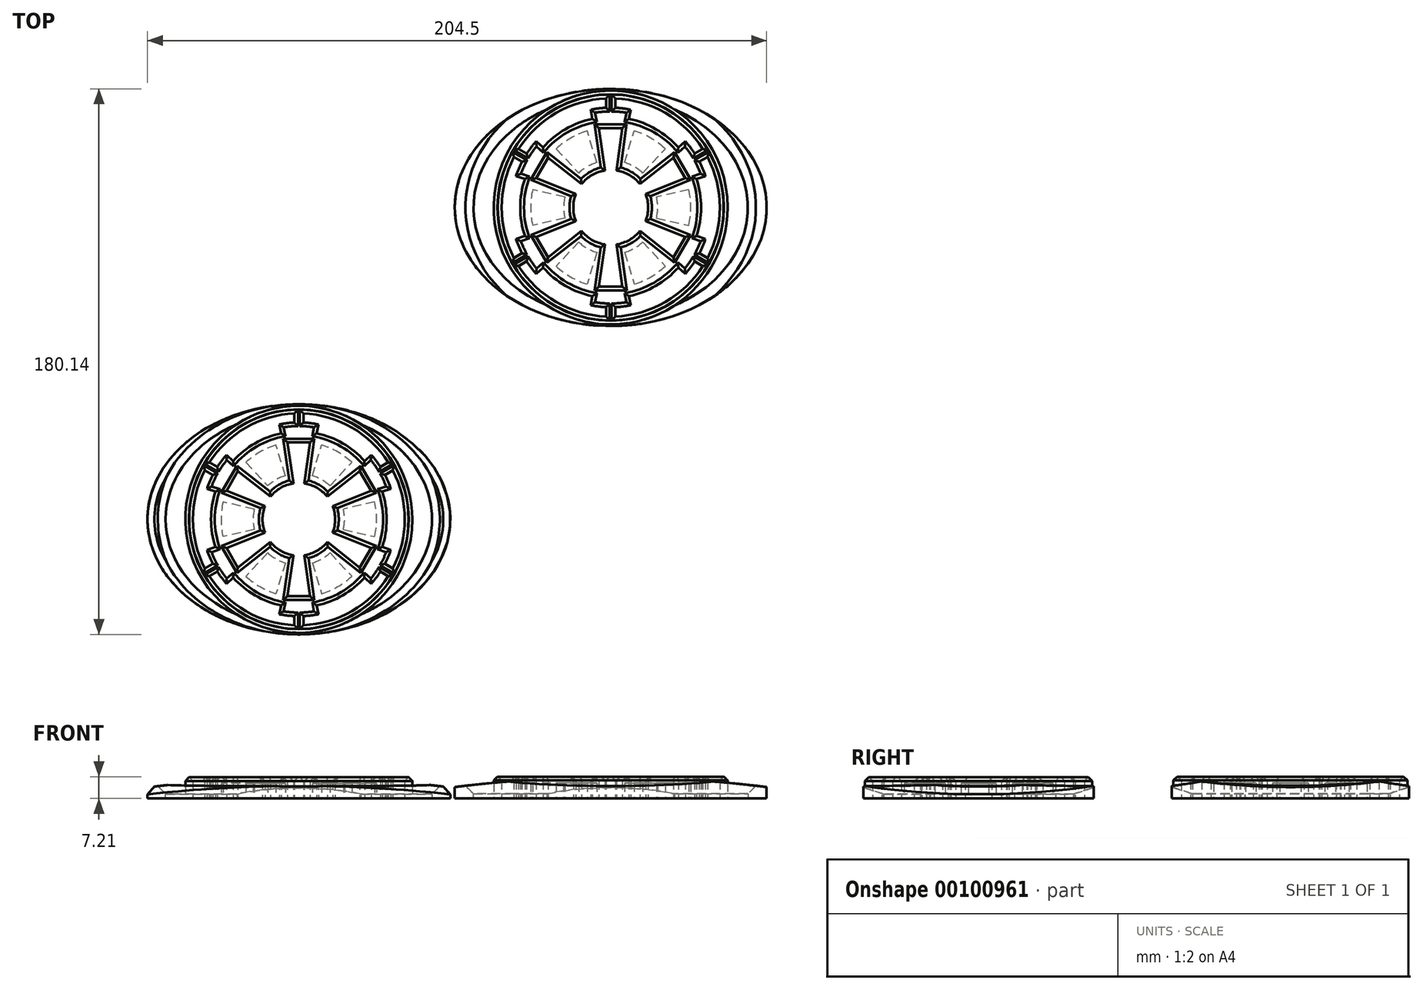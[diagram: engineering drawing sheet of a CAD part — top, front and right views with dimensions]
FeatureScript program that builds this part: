
annotation { "Feature Type Name" : "Feature", "Feature Type Description" : "" }
export const myFeature = defineFeature(function(context is Context, id is Id, definition is map)
    precondition{}
    {
        {
            var Q0;
            Q0=qCreatedBy(makeId("Top.planeOp"),FACE);
            var sketch = newSketch(context, id + "F0", { "sketchPlane" : qUnion([Q0])});
            skEllipse(sketch, "E0", {"center": v(0, 0) * mm, "majorRadius": 38 * mm, "minorRadius": 50 * mm, "majorAxis": v(0, 1)});
            skEllipse(sketch, "E1", {"center": v(0, 0) * mm, "majorRadius": 35.5 * mm, "minorRadius": 44 * mm, "majorAxis": v(0, 1)});
            skSolve(sketch);
        }
        {
            var Q0;
            Q0 = qSketchRegion(id + "F0", true);
            extrude(context, id + "F1", {"entities" : qUnion([Q0]), "depth" : 7 * mm});
        }
        {
            var Q0;
            Q0=makeQuery(id+"F1.opExtrude","CAP_EDGE",EDGE,{"disambiguationData":[OSD([sQuery(id+"F0.wireOp",EDGE,"E1")])],"isStart":false});
            chamfer(context, id + "F2", {"entities" : qUnion([Q0]), "width" : 5.5 * mm, "tangentPropagation" : true});
        }
        {
            var Q0;
            Q0=qCreatedBy(makeId("Front.planeOp"),FACE);
            var sketch = newSketch(context, id + "F3", { "sketchPlane" : qUnion([Q0])});
            skPoint(sketch, "E2.middle", {"position": v(0, 0) * mm});
            skArc(sketch, "E3", {"start": v(50.97, 3.54) * mm, "mid": v(0, 6.8) * mm, "end": v(-50.97, 3.54) * mm});
            skLineSegment(sketch, "E4.top", {"start": v(-50.97, 12) * mm, "end": v(50.97, 12) * mm});
            skLineSegment(sketch, "E4.left", {"start": v(-50.97, 3.54) * mm, "end": v(-50.97, 12) * mm});
            skLineSegment(sketch, "E4.right", {"start": v(50.97, 3.54) * mm, "end": v(50.97, 12) * mm});
            skPoint(sketch, "E2.right.end.orphan", {"position": v(-50.97, -3.54) * mm});
            skPoint(sketch, "E2.left.end.orphan", {"position": v(50.97, -3.54) * mm});
            skSolve(sketch);
        }
        {
            var Q0;
            Q0 = qSketchRegion(id + "F3", true);
            extrude(context, id + "F4", {"entities" : qUnion([Q0]), "operationType" : NewBodyOperationType.REMOVE, "endBound" : BoundingType.SYMMETRIC, "oppositeDirection" : true, "depth" : 100 * mm});
        }
        {
            var Q0;
            Q0=qCreatedBy(makeId("Top.planeOp"),FACE);
            var sketch = newSketch(context, id + "F5", { "sketchPlane" : qUnion([Q0])});
            skArc(sketch, "E5", {"start": v(0, 37.5) * mm, "mid": v(-35.71, 11.45) * mm, "end": v(-21.8, -30.51) * mm});
            skArc(sketch, "E6", {"start": v(-31.03, 16.18) * mm, "mid": v(-35, 0) * mm, "end": v(-31.03, -16.18) * mm});
            skLineSegment(sketch, "E7.left", {"start": v(-1.5, 34.98) * mm, "end": v(-1.5, 31.96) * mm});
            skLineSegment(sketch, "E7.right", {"start": v(1.5, 34.98) * mm, "end": v(1.5, 31.96) * mm});
            skLineSegment(sketch, "E8.1.0", {"start": v(-31.03, -16.18) * mm, "end": v(-28.43, -14.68) * mm});
            skLineSegment(sketch, "E8.1.1", {"start": v(-29.53, -18.78) * mm, "end": v(-26.93, -17.28) * mm});
            skLineSegment(sketch, "E8.2.0", {"start": v(29.53, -18.78) * mm, "end": v(26.93, -17.28) * mm});
            skLineSegment(sketch, "E8.2.1", {"start": v(31.03, -16.18) * mm, "end": v(28.43, -14.68) * mm});
            skArc(sketch, "E9", {"start": v(-28.43, 14.68) * mm, "mid": v(-29.37, 12.7) * mm, "end": v(-30.17, 10.66) * mm});
            skArc(sketch, "E10", {"start": v(-27.52, 9.14) * mm, "mid": v(-29, 0) * mm, "end": v(-27.52, -9.14) * mm});
            skPoint(sketch, "E11.orphan", {"position": v(-31.93, 16.7) * mm});
            skPoint(sketch, "E12.orphan", {"position": v(-30.43, 19.3) * mm});
            skPoint(sketch, "E13.orphan", {"position": v(-28.25, 23.07) * mm});
            skLineSegment(sketch, "E14.trimOffspring", {"start": v(-26.93, 17.28) * mm, "end": v(-29.53, 18.78) * mm});
            skLineSegment(sketch, "E15.trimOffspring", {"start": v(-28.43, 14.68) * mm, "end": v(-31.03, 16.18) * mm});
            skArc(sketch, "E16.trimOffspring", {"start": v(-30.17, -10.66) * mm, "mid": v(-29.37, -12.7) * mm, "end": v(-28.43, -14.68) * mm});
            skArc(sketch, "E17.trimOffspring", {"start": v(-24.32, 20.8) * mm, "mid": v(-25.69, 19.08) * mm, "end": v(-26.93, 17.28) * mm});
            skPoint(sketch, "E18.orphan", {"position": v(-5.85, 36) * mm});
            skPoint(sketch, "E19.orphan", {"position": v(1.5, 36) * mm});
            skPoint(sketch, "E20.orphan", {"position": v(-1.5, 36) * mm});
            skPoint(sketch, "E21.orphan", {"position": v(5.85, 36) * mm});
            skArc(sketch, "E22.trimOffspring", {"start": v(-21.8, -30.51) * mm, "mid": v(35.71, -11.45) * mm, "end": v(0, 37.5) * mm});
            skArc(sketch, "E23.trimOffspring", {"start": v(5.85, 31.46) * mm, "mid": v(3.68, 31.79) * mm, "end": v(1.5, 31.96) * mm});
            skArc(sketch, "E24.trimOffspring", {"start": v(-5.85, 28.4) * mm, "mid": v(-14.5, 25.11) * mm, "end": v(-21.67, 19.27) * mm});
            skArc(sketch, "E25.trimOffspring", {"start": v(-1.5, 34.97) * mm, "mid": v(-17.5, 30.31) * mm, "end": v(-29.53, 18.78) * mm});
            skArc(sketch, "E26.trimOffspring", {"start": v(-1.5, 31.96) * mm, "mid": v(-3.68, 31.79) * mm, "end": v(-5.85, 31.46) * mm});
            skArc(sketch, "E27.trimOffspring", {"start": v(21.67, 19.27) * mm, "mid": v(14.5, 25.11) * mm, "end": v(5.85, 28.4) * mm});
            skPoint(sketch, "E28.orphan", {"position": v(30.43, 19.3) * mm});
            skPoint(sketch, "E29.orphan", {"position": v(31.93, 16.7) * mm});
            skPoint(sketch, "E30.orphan", {"position": v(34.1, 12.93) * mm});
            skLineSegment(sketch, "E31.trimOffspring", {"start": v(26.93, 17.28) * mm, "end": v(29.53, 18.78) * mm});
            skLineSegment(sketch, "E32.trimOffspring", {"start": v(28.43, 14.68) * mm, "end": v(31.03, 16.18) * mm});
            skArc(sketch, "E33.trimOffspring", {"start": v(26.93, 17.28) * mm, "mid": v(25.69, 19.08) * mm, "end": v(24.32, 20.8) * mm});
            skArc(sketch, "E34.trimOffspring", {"start": v(29.53, 18.78) * mm, "mid": v(17.5, 30.31) * mm, "end": v(1.5, 34.97) * mm});
            skArc(sketch, "E35.trimOffspring", {"start": v(30.17, 10.66) * mm, "mid": v(29.37, 12.7) * mm, "end": v(28.43, 14.68) * mm});
            skPoint(sketch, "E36.orphan", {"position": v(34.1, -12.93) * mm});
            skArc(sketch, "E37.trimOffspring", {"start": v(27.52, -9.14) * mm, "mid": v(29, 0) * mm, "end": v(27.52, 9.14) * mm});
            skArc(sketch, "E38.trimOffspring", {"start": v(28.43, -14.68) * mm, "mid": v(29.37, -12.7) * mm, "end": v(30.17, -10.66) * mm});
            skPoint(sketch, "E39.orphan", {"position": v(31.93, -16.7) * mm});
            skPoint(sketch, "E40.orphan", {"position": v(30.43, -19.3) * mm});
            skArc(sketch, "E41.trimOffspring", {"start": v(24.32, -20.8) * mm, "mid": v(25.69, -19.08) * mm, "end": v(26.93, -17.28) * mm});
            skArc(sketch, "E42.trimOffspring", {"start": v(5.85, -28.4) * mm, "mid": v(14.5, -25.11) * mm, "end": v(21.67, -19.27) * mm});
            skLineSegment(sketch, "E43.trimOffspring", {"start": v(-1.5, -31.96) * mm, "end": v(-1.5, -34.98) * mm});
            skLineSegment(sketch, "E44.trimOffspring", {"start": v(1.5, -31.96) * mm, "end": v(1.5, -34.97) * mm});
            skArc(sketch, "E45.trimOffspring", {"start": v(1.5, -31.96) * mm, "mid": v(3.68, -31.79) * mm, "end": v(5.85, -31.46) * mm});
            skPoint(sketch, "E46.orphan", {"position": v(5.85, -36) * mm});
            skArc(sketch, "E47.trimOffspring", {"start": v(1.5, -34.97) * mm, "mid": v(17.5, -30.31) * mm, "end": v(29.53, -18.78) * mm});
            skPoint(sketch, "E48.orphan", {"position": v(-1.5, -36) * mm});
            skPoint(sketch, "E49.trimOffspring.end.orphan", {"position": v(-5.85, -36) * mm});
            skPoint(sketch, "E50.top.end.orphan", {"position": v(1.5, -36) * mm});
            skPoint(sketch, "E51.orphan", {"position": v(-34.1, -12.93) * mm});
            skPoint(sketch, "E52.orphan", {"position": v(-31.93, -16.7) * mm});
            skPoint(sketch, "E53.orphan", {"position": v(-30.43, -19.3) * mm});
            skPoint(sketch, "E54.orphan", {"position": v(-28.25, -23.07) * mm});
            skArc(sketch, "E55.trimOffspring", {"start": v(-29.53, -18.78) * mm, "mid": v(-17.5, -30.31) * mm, "end": v(-1.5, -34.97) * mm});
            skArc(sketch, "E56.trimOffspring", {"start": v(-26.93, -17.28) * mm, "mid": v(-25.69, -19.08) * mm, "end": v(-24.32, -20.8) * mm});
            skArc(sketch, "E57.trimOffspring", {"start": v(-21.67, -19.27) * mm, "mid": v(-14.5, -25.11) * mm, "end": v(-5.85, -28.4) * mm});
            skArc(sketch, "E58", {"start": v(-1.82, 11.86) * mm, "mid": v(-6, 10.4) * mm, "end": v(-9.36, 7.5) * mm});
            skLineSegment(sketch, "E59.bottom", {"start": v(-3.75, 25.42) * mm, "end": v(3.75, 25.42) * mm});
            skLineSegment(sketch, "E59.top", {"start": v(-3.75, -25.42) * mm, "end": v(3.75, -25.42) * mm});
            skLineSegment(sketch, "E60", {"start": v(-3.75, 25.42) * mm, "end": v(-1.82, 11.86) * mm});
            skLineSegment(sketch, "E61", {"start": v(3.75, 25.42) * mm, "end": v(1.82, 11.86) * mm});
            skLineSegment(sketch, "E62", {"start": v(-3.75, -25.42) * mm, "end": v(-1.82, -11.86) * mm});
            skLineSegment(sketch, "E63", {"start": v(3.75, -25.42) * mm, "end": v(1.82, -11.86) * mm});
            skLineSegment(sketch, "E64.1.0", {"start": v(-20.13, -15.96) * mm, "end": v(-23.88, -9.46) * mm});
            skLineSegment(sketch, "E64.1.1", {"start": v(-23.88, -9.46) * mm, "end": v(-11.18, -4.35) * mm});
            skLineSegment(sketch, "E64.1.2", {"start": v(-20.13, -15.96) * mm, "end": v(-9.36, -7.5) * mm});
            skLineSegment(sketch, "E64.1.3", {"start": v(23.88, 9.46) * mm, "end": v(20.13, 15.96) * mm});
            skLineSegment(sketch, "E64.1.4", {"start": v(20.13, 15.96) * mm, "end": v(9.36, 7.5) * mm});
            skLineSegment(sketch, "E64.1.5", {"start": v(23.88, 9.46) * mm, "end": v(11.18, 4.35) * mm});
            skLineSegment(sketch, "E64.2.0", {"start": v(23.89, -9.46) * mm, "end": v(20.14, -15.95) * mm});
            skLineSegment(sketch, "E64.2.1", {"start": v(20.14, -15.95) * mm, "end": v(9.36, -7.5) * mm});
            skLineSegment(sketch, "E64.2.2", {"start": v(23.89, -9.46) * mm, "end": v(11.18, -4.35) * mm});
            skLineSegment(sketch, "E64.2.3", {"start": v(-20.14, 15.95) * mm, "end": v(-23.89, 9.46) * mm});
            skLineSegment(sketch, "E64.2.4", {"start": v(-23.89, 9.46) * mm, "end": v(-11.18, 4.35) * mm});
            skLineSegment(sketch, "E64.2.5", {"start": v(-20.14, 15.95) * mm, "end": v(-9.36, 7.5) * mm});
            skArc(sketch, "E65.trimOffspring", {"start": v(9.36, 7.5) * mm, "mid": v(6, 10.4) * mm, "end": v(1.82, 11.86) * mm});
            skArc(sketch, "E66.trimOffspring", {"start": v(11.18, -4.35) * mm, "mid": v(12, 0) * mm, "end": v(11.18, 4.35) * mm});
            skArc(sketch, "E67.trimOffspring", {"start": v(1.82, -11.86) * mm, "mid": v(6, -10.4) * mm, "end": v(9.36, -7.5) * mm});
            skArc(sketch, "E68.trimOffspring", {"start": v(-9.36, -7.5) * mm, "mid": v(-6, -10.4) * mm, "end": v(-1.82, -11.86) * mm});
            skArc(sketch, "E69.trimOffspring", {"start": v(-11.18, 4.35) * mm, "mid": v(-12, 0) * mm, "end": v(-11.18, -4.35) * mm});
            skLineSegment(sketch, "E70", {"start": v(6.46, 31.34) * mm, "end": v(5.85, 28.4) * mm});
            skLineSegment(sketch, "E71", {"start": v(-6.46, 31.34) * mm, "end": v(-5.85, 28.4) * mm});
            skLineSegment(sketch, "E72", {"start": v(23.92, -21.26) * mm, "end": v(21.67, -19.27) * mm});
            skLineSegment(sketch, "E73", {"start": v(-30.37, 10.08) * mm, "end": v(-27.52, 9.14) * mm});
            skLineSegment(sketch, "E74", {"start": v(30.37, 10.08) * mm, "end": v(27.52, 9.14) * mm});
            skLineSegment(sketch, "E75", {"start": v(-23.92, -21.26) * mm, "end": v(-21.67, -19.27) * mm});
            skArc(sketch, "E76.converted", {"start": v(-6.46, -31.34) * mm, "mid": v(-3.99, -31.75) * mm, "end": v(-1.5, -31.96) * mm});
            skArc(sketch, "E77.trimOffspring", {"start": v(23.92, -21.26) * mm, "mid": v(25.5, -19.33) * mm, "end": v(26.93, -17.28) * mm});
            skLineSegment(sketch, "E78.trimOffspring", {"start": v(-5.85, -28.4) * mm, "end": v(-6.5, -31.52) * mm});
            skLineSegment(sketch, "E79.trimOffspring", {"start": v(5.85, -28.4) * mm, "end": v(6.46, -31.34) * mm});
            skArc(sketch, "E80.trimOffspring", {"start": v(30.37, 10.08) * mm, "mid": v(29.5, 12.42) * mm, "end": v(28.43, 14.68) * mm});
            skLineSegment(sketch, "E81.trimOffspring", {"start": v(27.52, -9.14) * mm, "end": v(30.37, -10.08) * mm});
            skLineSegment(sketch, "E82.trimOffspring", {"start": v(21.67, 19.27) * mm, "end": v(23.92, 21.26) * mm});
            skArc(sketch, "E83.trimOffspring", {"start": v(6.46, 31.34) * mm, "mid": v(3.99, 31.75) * mm, "end": v(1.5, 31.96) * mm});
            skArc(sketch, "E84.trimOffspring", {"start": v(-23.92, 21.26) * mm, "mid": v(-25.5, 19.33) * mm, "end": v(-26.93, 17.28) * mm});
            skLineSegment(sketch, "E85.trimOffspring", {"start": v(-21.67, 19.27) * mm, "end": v(-23.92, 21.26) * mm});
            skArc(sketch, "E86.trimOffspring", {"start": v(-30.37, -10.08) * mm, "mid": v(-29.5, -12.42) * mm, "end": v(-28.43, -14.68) * mm});
            skLineSegment(sketch, "E87.trimOffspring", {"start": v(-27.52, -9.14) * mm, "end": v(-30.37, -10.08) * mm});
            skArc(sketch, "E88.trimOffspring", {"start": v(1.5, -31.96) * mm, "mid": v(3.99, -31.75) * mm, "end": v(6.46, -31.34) * mm});
            skArc(sketch, "E89.trimOffspring", {"start": v(28.43, -14.68) * mm, "mid": v(29.5, -12.42) * mm, "end": v(30.37, -10.08) * mm});
            skArc(sketch, "E90.trimOffspring", {"start": v(26.93, 17.28) * mm, "mid": v(25.5, 19.33) * mm, "end": v(23.92, 21.26) * mm});
            skArc(sketch, "E91.trimOffspring", {"start": v(-1.5, 31.96) * mm, "mid": v(-3.99, 31.75) * mm, "end": v(-6.46, 31.34) * mm});
            skArc(sketch, "E92.trimOffspring", {"start": v(-28.43, 14.68) * mm, "mid": v(-29.5, 12.42) * mm, "end": v(-30.37, 10.08) * mm});
            skArc(sketch, "E93.trimOffspring", {"start": v(-26.93, -17.28) * mm, "mid": v(-25.5, -19.33) * mm, "end": v(-23.92, -21.26) * mm});
            skArc(sketch, "E94.trimOffspring", {"start": v(31.03, -16.18) * mm, "mid": v(35, 0) * mm, "end": v(31.03, 16.18) * mm});
            skSolve(sketch);
        }
        {
            var Q0;
            Q0 = qSketchRegion(id + "F5", true);
            extrude(context, id + "F6", {"entities" : qUnion([Q0]), "operationType" : NewBodyOperationType.ADD, "depth" : 7 * mm});
        }
        {
            var Q0;
            Q0=makeQuery(id+"F6.boolean.opBoolean","MERGE",FACE,{"derivedFrom":[makeQuery(id+"F1.opExtrude","CAP_FACE",FACE,{"disambiguationData":[OSD([sQuery(id+"F0.wireOp",EDGE,"E0"),sQuery(id+"F0.wireOp",EDGE,"E1")])],"isStart":true}),makeQuery(id+"F6.opExtrude","CAP_FACE",FACE,{"disambiguationData":[OSD([sQuery(id+"F5.wireOp",EDGE,"E5"),sQuery(id+"F5.wireOp",EDGE,"E6"),sQuery(id+"F5.wireOp",EDGE,"E7.left"),sQuery(id+"F5.wireOp",EDGE,"E7.right"),sQuery(id+"F5.wireOp",EDGE,"E8.1.0"),sQuery(id+"F5.wireOp",EDGE,"E8.1.1"),sQuery(id+"F5.wireOp",EDGE,"E8.2.0"),sQuery(id+"F5.wireOp",EDGE,"E8.2.1"),sQuery(id+"F5.wireOp",EDGE,"E10"),sQuery(id+"F5.wireOp",EDGE,"E14.trimOffspring"),sQuery(id+"F5.wireOp",EDGE,"E15.trimOffspring"),sQuery(id+"F5.wireOp",EDGE,"E22.trimOffspring"),sQuery(id+"F5.wireOp",EDGE,"E24.trimOffspring"),sQuery(id+"F5.wireOp",EDGE,"E25.trimOffspring"),sQuery(id+"F5.wireOp",EDGE,"E27.trimOffspring"),sQuery(id+"F5.wireOp",EDGE,"E31.trimOffspring"),sQuery(id+"F5.wireOp",EDGE,"E32.trimOffspring"),sQuery(id+"F5.wireOp",EDGE,"E34.trimOffspring"),sQuery(id+"F5.wireOp",EDGE,"E37.trimOffspring"),sQuery(id+"F5.wireOp",EDGE,"E42.trimOffspring"),sQuery(id+"F5.wireOp",EDGE,"E43.trimOffspring"),sQuery(id+"F5.wireOp",EDGE,"E44.trimOffspring"),sQuery(id+"F5.wireOp",EDGE,"E47.trimOffspring"),sQuery(id+"F5.wireOp",EDGE,"E55.trimOffspring"),sQuery(id+"F5.wireOp",EDGE,"E57.trimOffspring"),sQuery(id+"F5.wireOp",EDGE,"E58"),sQuery(id+"F5.wireOp",EDGE,"E59.bottom"),sQuery(id+"F5.wireOp",EDGE,"E59.top"),sQuery(id+"F5.wireOp",EDGE,"E60"),sQuery(id+"F5.wireOp",EDGE,"E61"),sQuery(id+"F5.wireOp",EDGE,"E62"),sQuery(id+"F5.wireOp",EDGE,"E63"),sQuery(id+"F5.wireOp",EDGE,"E64.1.0"),sQuery(id+"F5.wireOp",EDGE,"E64.1.1"),sQuery(id+"F5.wireOp",EDGE,"E64.1.2"),sQuery(id+"F5.wireOp",EDGE,"E64.1.3"),sQuery(id+"F5.wireOp",EDGE,"E64.1.4"),sQuery(id+"F5.wireOp",EDGE,"E64.1.5"),sQuery(id+"F5.wireOp",EDGE,"E64.2.0"),sQuery(id+"F5.wireOp",EDGE,"E64.2.1"),sQuery(id+"F5.wireOp",EDGE,"E64.2.2"),sQuery(id+"F5.wireOp",EDGE,"E64.2.3"),sQuery(id+"F5.wireOp",EDGE,"E64.2.4"),sQuery(id+"F5.wireOp",EDGE,"E64.2.5"),sQuery(id+"F5.wireOp",EDGE,"E65.trimOffspring"),sQuery(id+"F5.wireOp",EDGE,"E66.trimOffspring"),sQuery(id+"F5.wireOp",EDGE,"E67.trimOffspring"),sQuery(id+"F5.wireOp",EDGE,"E68.trimOffspring"),sQuery(id+"F5.wireOp",EDGE,"E69.trimOffspring"),sQuery(id+"F5.wireOp",EDGE,"E70"),sQuery(id+"F5.wireOp",EDGE,"E71"),sQuery(id+"F5.wireOp",EDGE,"E72"),sQuery(id+"F5.wireOp",EDGE,"E73"),sQuery(id+"F5.wireOp",EDGE,"E74"),sQuery(id+"F5.wireOp",EDGE,"E75"),sQuery(id+"F5.wireOp",EDGE,"E76.converted"),sQuery(id+"F5.wireOp",EDGE,"E77.trimOffspring"),sQuery(id+"F5.wireOp",EDGE,"E78.trimOffspring"),sQuery(id+"F5.wireOp",EDGE,"E79.trimOffspring"),sQuery(id+"F5.wireOp",EDGE,"E80.trimOffspring"),sQuery(id+"F5.wireOp",EDGE,"E81.trimOffspring"),sQuery(id+"F5.wireOp",EDGE,"E82.trimOffspring"),sQuery(id+"F5.wireOp",EDGE,"E83.trimOffspring"),sQuery(id+"F5.wireOp",EDGE,"E84.trimOffspring"),sQuery(id+"F5.wireOp",EDGE,"E85.trimOffspring"),sQuery(id+"F5.wireOp",EDGE,"E86.trimOffspring"),sQuery(id+"F5.wireOp",EDGE,"E87.trimOffspring"),sQuery(id+"F5.wireOp",EDGE,"E88.trimOffspring"),sQuery(id+"F5.wireOp",EDGE,"E89.trimOffspring"),sQuery(id+"F5.wireOp",EDGE,"E90.trimOffspring"),sQuery(id+"F5.wireOp",EDGE,"E91.trimOffspring"),sQuery(id+"F5.wireOp",EDGE,"E92.trimOffspring"),sQuery(id+"F5.wireOp",EDGE,"E93.trimOffspring"),sQuery(id+"F5.wireOp",EDGE,"E94.trimOffspring")])],"isStart":true})]});
            var sketch = newSketch(context, id + "F7", { "sketchPlane" : qUnion([Q0])});
            skArc(sketch, "E95", {"start": v(-17.5, -18.82) * mm, "mid": v(-12.85, -22.25) * mm, "end": v(-7.56, -24.55) * mm});
            skArc(sketch, "E96", {"start": v(-4.43, 14.42) * mm, "mid": v(-7.54, 13.07) * mm, "end": v(-10.27, 11.05) * mm});
            skLineSegment(sketch, "E97", {"start": v(4.44, 14.42) * mm, "end": v(7.56, 24.55) * mm});
            skLineSegment(sketch, "E98", {"start": v(10.27, 11.05) * mm, "end": v(17.5, 18.82) * mm});
            skLineSegment(sketch, "E99.1.0", {"start": v(-14.7, -3.36) * mm, "end": v(-25.04, -5.73) * mm});
            skLineSegment(sketch, "E99.1.1", {"start": v(-14.7, 3.37) * mm, "end": v(-25.04, 5.74) * mm});
            skLineSegment(sketch, "E99.2.0", {"start": v(10.27, -11.05) * mm, "end": v(17.48, -18.82) * mm});
            skLineSegment(sketch, "E99.2.1", {"start": v(4.43, -14.42) * mm, "end": v(7.55, -24.56) * mm});
            skLineSegment(sketch, "E100", {"start": v(-4.43, 14.42) * mm, "end": v(-7.55, 24.56) * mm});
            skLineSegment(sketch, "E101", {"start": v(-7.55, 24.56) * mm, "end": v(-4.43, 14.42) * mm});
            skLineSegment(sketch, "E102", {"start": v(-10.27, 11.05) * mm, "end": v(-17.48, 18.82) * mm});
            skLineSegment(sketch, "E103.1.0", {"start": v(-4.44, -14.42) * mm, "end": v(-7.56, -24.55) * mm});
            skLineSegment(sketch, "E103.1.1", {"start": v(-17.5, -18.82) * mm, "end": v(-10.27, -11.05) * mm});
            skLineSegment(sketch, "E103.2.0", {"start": v(14.7, 3.36) * mm, "end": v(25.04, 5.73) * mm});
            skLineSegment(sketch, "E103.2.1", {"start": v(25.04, -5.74) * mm, "end": v(14.7, -3.37) * mm});
            skArc(sketch, "E104.trimOffspring", {"start": v(10.27, 11.05) * mm, "mid": v(7.55, 13.06) * mm, "end": v(4.44, 14.42) * mm});
            skArc(sketch, "E105.trimOffspring", {"start": v(14.7, -3.37) * mm, "mid": v(15.09, 0) * mm, "end": v(14.7, 3.36) * mm});
            skArc(sketch, "E106.trimOffspring", {"start": v(4.43, -14.42) * mm, "mid": v(7.54, -13.07) * mm, "end": v(10.27, -11.05) * mm});
            skArc(sketch, "E107.trimOffspring", {"start": v(-10.27, -11.05) * mm, "mid": v(-7.55, -13.06) * mm, "end": v(-4.44, -14.42) * mm});
            skArc(sketch, "E108.trimOffspring", {"start": v(7.55, -24.56) * mm, "mid": v(12.84, -22.25) * mm, "end": v(17.48, -18.82) * mm});
            skArc(sketch, "E109.trimOffspring", {"start": v(25.04, -5.74) * mm, "mid": v(25.69, 0) * mm, "end": v(25.04, 5.73) * mm});
            skArc(sketch, "E110.trimOffspring", {"start": v(-25.04, 5.74) * mm, "mid": v(-25.69, 0) * mm, "end": v(-25.04, -5.73) * mm});
            skArc(sketch, "E111.trimOffspring", {"start": v(-14.7, 3.37) * mm, "mid": v(-15.09, 0) * mm, "end": v(-14.7, -3.36) * mm});
            skArc(sketch, "E112.trimOffspring", {"start": v(-7.55, 24.56) * mm, "mid": v(-12.84, 22.25) * mm, "end": v(-17.48, 18.82) * mm});
            skArc(sketch, "E113.trimOffspring", {"start": v(17.5, 18.82) * mm, "mid": v(12.85, 22.25) * mm, "end": v(7.56, 24.55) * mm});
            skSolve(sketch);
        }
        {
            var Q0;
            Q0 = qSketchRegion(id + "F7", true);
            extrude(context, id + "F8", {"entities" : qUnion([Q0]), "operationType" : NewBodyOperationType.REMOVE, "oppositeDirection" : true, "depth" : 5 * mm});
        }
        {
            var Q0;
            Q0=makeQuery(id+"F6.opExtrude","CAP_FACE",FACE,{"disambiguationData":[OSD([sQuery(id+"F5.wireOp",EDGE,"E5"),sQuery(id+"F5.wireOp",EDGE,"E6"),sQuery(id+"F5.wireOp",EDGE,"E7.left"),sQuery(id+"F5.wireOp",EDGE,"E7.right"),sQuery(id+"F5.wireOp",EDGE,"E8.1.0"),sQuery(id+"F5.wireOp",EDGE,"E8.1.1"),sQuery(id+"F5.wireOp",EDGE,"E8.2.0"),sQuery(id+"F5.wireOp",EDGE,"E8.2.1"),sQuery(id+"F5.wireOp",EDGE,"E10"),sQuery(id+"F5.wireOp",EDGE,"E14.trimOffspring"),sQuery(id+"F5.wireOp",EDGE,"E15.trimOffspring"),sQuery(id+"F5.wireOp",EDGE,"E22.trimOffspring"),sQuery(id+"F5.wireOp",EDGE,"E24.trimOffspring"),sQuery(id+"F5.wireOp",EDGE,"E25.trimOffspring"),sQuery(id+"F5.wireOp",EDGE,"E27.trimOffspring"),sQuery(id+"F5.wireOp",EDGE,"E31.trimOffspring"),sQuery(id+"F5.wireOp",EDGE,"E32.trimOffspring"),sQuery(id+"F5.wireOp",EDGE,"E34.trimOffspring"),sQuery(id+"F5.wireOp",EDGE,"E37.trimOffspring"),sQuery(id+"F5.wireOp",EDGE,"E42.trimOffspring"),sQuery(id+"F5.wireOp",EDGE,"E43.trimOffspring"),sQuery(id+"F5.wireOp",EDGE,"E44.trimOffspring"),sQuery(id+"F5.wireOp",EDGE,"E47.trimOffspring"),sQuery(id+"F5.wireOp",EDGE,"E55.trimOffspring"),sQuery(id+"F5.wireOp",EDGE,"E57.trimOffspring"),sQuery(id+"F5.wireOp",EDGE,"E58"),sQuery(id+"F5.wireOp",EDGE,"E59.bottom"),sQuery(id+"F5.wireOp",EDGE,"E59.top"),sQuery(id+"F5.wireOp",EDGE,"E60"),sQuery(id+"F5.wireOp",EDGE,"E61"),sQuery(id+"F5.wireOp",EDGE,"E62"),sQuery(id+"F5.wireOp",EDGE,"E63"),sQuery(id+"F5.wireOp",EDGE,"E64.1.0"),sQuery(id+"F5.wireOp",EDGE,"E64.1.1"),sQuery(id+"F5.wireOp",EDGE,"E64.1.2"),sQuery(id+"F5.wireOp",EDGE,"E64.1.3"),sQuery(id+"F5.wireOp",EDGE,"E64.1.4"),sQuery(id+"F5.wireOp",EDGE,"E64.1.5"),sQuery(id+"F5.wireOp",EDGE,"E64.2.0"),sQuery(id+"F5.wireOp",EDGE,"E64.2.1"),sQuery(id+"F5.wireOp",EDGE,"E64.2.2"),sQuery(id+"F5.wireOp",EDGE,"E64.2.3"),sQuery(id+"F5.wireOp",EDGE,"E64.2.4"),sQuery(id+"F5.wireOp",EDGE,"E64.2.5"),sQuery(id+"F5.wireOp",EDGE,"E65.trimOffspring"),sQuery(id+"F5.wireOp",EDGE,"E66.trimOffspring"),sQuery(id+"F5.wireOp",EDGE,"E67.trimOffspring"),sQuery(id+"F5.wireOp",EDGE,"E68.trimOffspring"),sQuery(id+"F5.wireOp",EDGE,"E69.trimOffspring"),sQuery(id+"F5.wireOp",EDGE,"E70"),sQuery(id+"F5.wireOp",EDGE,"E71"),sQuery(id+"F5.wireOp",EDGE,"E72"),sQuery(id+"F5.wireOp",EDGE,"E73"),sQuery(id+"F5.wireOp",EDGE,"E74"),sQuery(id+"F5.wireOp",EDGE,"E75"),sQuery(id+"F5.wireOp",EDGE,"E76.converted"),sQuery(id+"F5.wireOp",EDGE,"E77.trimOffspring"),sQuery(id+"F5.wireOp",EDGE,"E78.trimOffspring"),sQuery(id+"F5.wireOp",EDGE,"E79.trimOffspring"),sQuery(id+"F5.wireOp",EDGE,"E80.trimOffspring"),sQuery(id+"F5.wireOp",EDGE,"E81.trimOffspring"),sQuery(id+"F5.wireOp",EDGE,"E82.trimOffspring"),sQuery(id+"F5.wireOp",EDGE,"E83.trimOffspring"),sQuery(id+"F5.wireOp",EDGE,"E84.trimOffspring"),sQuery(id+"F5.wireOp",EDGE,"E85.trimOffspring"),sQuery(id+"F5.wireOp",EDGE,"E86.trimOffspring"),sQuery(id+"F5.wireOp",EDGE,"E87.trimOffspring"),sQuery(id+"F5.wireOp",EDGE,"E88.trimOffspring"),sQuery(id+"F5.wireOp",EDGE,"E89.trimOffspring"),sQuery(id+"F5.wireOp",EDGE,"E90.trimOffspring"),sQuery(id+"F5.wireOp",EDGE,"E91.trimOffspring"),sQuery(id+"F5.wireOp",EDGE,"E92.trimOffspring"),sQuery(id+"F5.wireOp",EDGE,"E93.trimOffspring"),sQuery(id+"F5.wireOp",EDGE,"E94.trimOffspring")])],"isStart":false});
            chamfer(context, id + "F9", {"entities" : qUnion([Q0]), "width" : 1.2 * mm, "tangentPropagation" : true});
        }
        {
            var Q0;
            Q0=makeQuery(id+"F1.opExtrude","SWEPT_BODY",BODY,{"disambiguationData":[OSD([sQuery(id+"F0.wireOp",EDGE,"E0"),sQuery(id+"F0.wireOp",EDGE,"E1")])]});
            transform(context, id + "F10", {"entities" : qUnion([Q0]), "transformType" : TransformType.TRANSLATION_3D, "dx" : 100 * mm, "dy" : 100 * mm, "dz" : 0 * mm, "makeCopy" : true});
        }
        {
            var Q0;
            Q0=makeQuery(id+"F10.opPattern","COPY",BODY,{"derivedFrom":makeQuery(id+"F1.opExtrude","SWEPT_BODY",BODY,{"disambiguationData":[OSD([sQuery(id+"F0.wireOp",EDGE,"E0"),sQuery(id+"F0.wireOp",EDGE,"E1")])]}),"instanceName":"1"});
            var Q1;
            Q1=qCreatedBy(makeId("Origin.pointOp"),VERTEX);
            transform(context, id + "F11", {"entities" : qUnion([Q0]), "transformType" : TransformType.SCALE_UNIFORMLY, "scale" : 1.03, "scalePoint" : qUnion([Q1]), "makeCopy" : false});
        }
        {
            var Q0;
            Q0=makeQuery(id+"F4.boolean.opBoolean","INTERSECT",EDGE,{"disambiguationData":[OD(1.0)],"derivedFrom":[makeQuery(id+"F1.opExtrude","SWEPT_FACE",FACE,{"disambiguationData":[OSD([sQuery(id+"F0.wireOp",EDGE,"E0")])]}),makeQuery(id+"F4.opExtrude","SWEPT_FACE",FACE,{"disambiguationData":[OSD([sQuery(id+"F3.wireOp",EDGE,"E3")])]})]});
            var Q1;
            Q1=makeQuery(id+"F4.boolean.opBoolean","INTERSECT",EDGE,{"disambiguationData":[OD(0.0)],"derivedFrom":[makeQuery(id+"F1.opExtrude","SWEPT_FACE",FACE,{"disambiguationData":[OSD([sQuery(id+"F0.wireOp",EDGE,"E0")])]}),makeQuery(id+"F4.opExtrude","SWEPT_FACE",FACE,{"disambiguationData":[OSD([sQuery(id+"F3.wireOp",EDGE,"E3")])]})]});
            chamfer(context, id + "F12", {"entities" : qUnion([Q0, Q1]), "width" : 2.6 * mm, "tangentPropagation" : true});
        }
    });
